# Revit family: Haworth_Riverbend_Ottoman_EU_PRELIMINARY
name_source: partatom
category: Furniture
revit_build: Autodesk Revit 2018 (Build: 20170223_1515(x64)
units: mm (PartAtom-declared; Revit-internal decimal feet)

## family parameters
Always vertical = Yes
Cut with Voids When Loaded = No
OmniClass Number = 23.40.70.14.64.21
OmniClass Title = Systems Furniture
Room Calculation Point = No
Shared = No
Work Plane-Based = No

## types (4) — shared parameters
Actual Height = 43 cm
Assembly Code = E2020200
Custom Size = No
Custom Width = No
Description = Haworth - Riverbend - Ottoman
Manufacturer = Haworth
Max. Depth = 120 cm
Max. Width = 170 cm
Min. Depth = 65 cm
Min. Width = 65 cm
Model = SETSXX
Revision Number = 1
Size = Verify Final Dim. w/ Haworth
Trim Finish = Haworth _ Paint _ Plaster
URL = https://www.haworth.com
URL - Product = https://www.haworth.com
Warranty = http://www.haworth.com

## per-type parameters (varying)
| type | Actual Depth | Actual Width | Depth | Large Square | Medium Square | Rectangle | Small Square | Width |
| 85 x 85 x 43 | 85 cm | 85 cm | 85 cm | No | Yes | No | No | 85 cm |
| 120 x 120 x 43 | 120 cm | 120 cm | 120 cm | Yes | No | No | No | 120 cm |
| 85 x 170 x 43 | 85 cm | 170 cm | 85 cm | No | No | Yes | No | 170 cm |
| 65 x 65 x 43 | 65 cm | 65 cm | 65 cm | No | No | No | Yes | 65 cm |

## geometry (parser evidence)
native form markers: Sweep x3
no freeform markers — native parametric forms only
